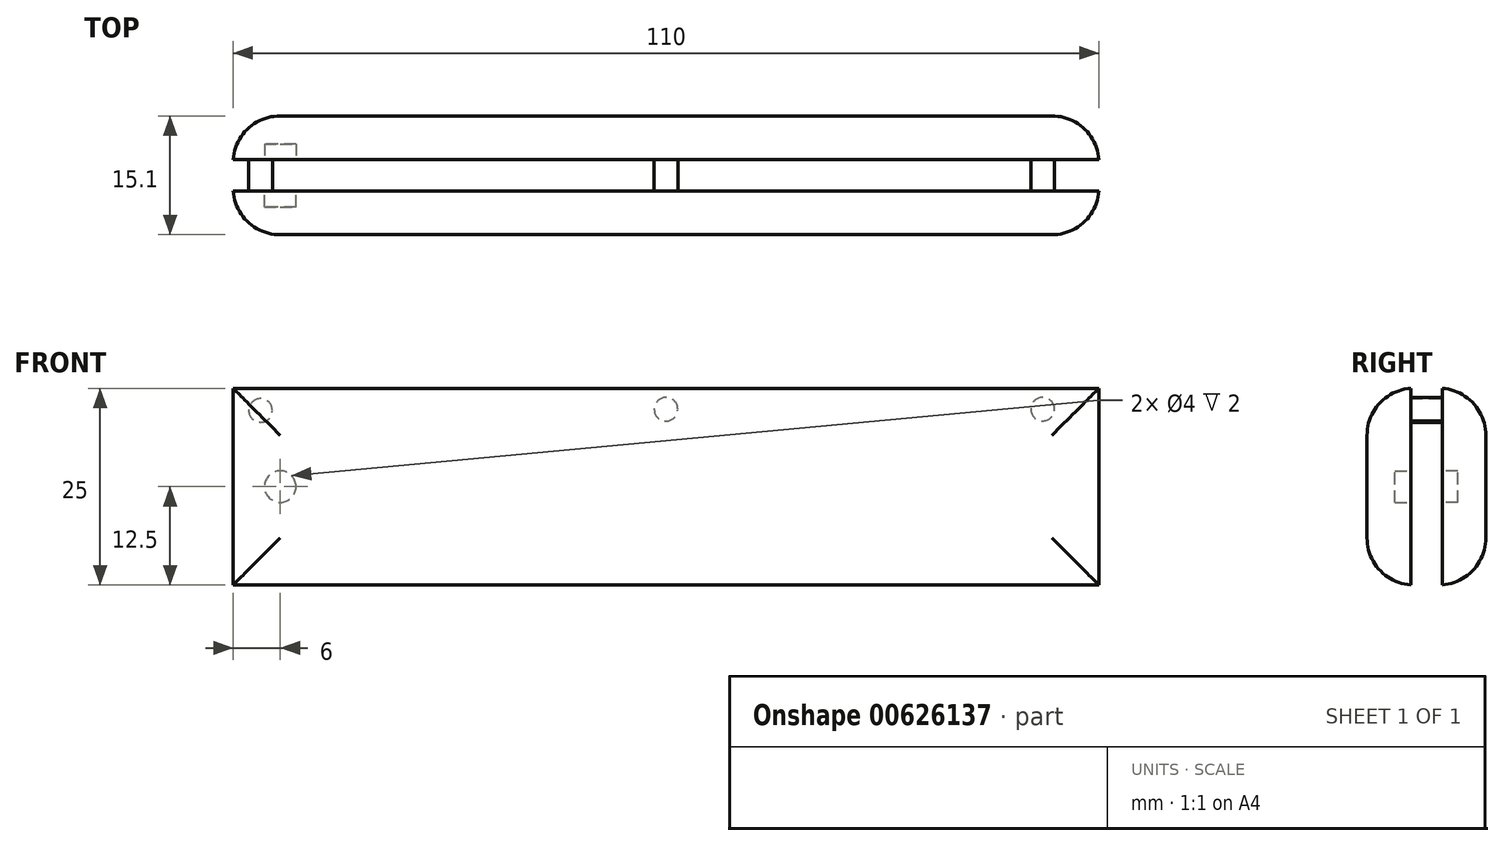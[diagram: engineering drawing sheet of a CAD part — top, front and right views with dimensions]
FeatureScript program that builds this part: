
annotation { "Feature Type Name" : "Feature", "Feature Type Description" : "" }
export const myFeature = defineFeature(function(context is Context, id is Id, definition is map)
    precondition{}
    {
        {
            var Q0;
            Q0=qCreatedBy(makeId("Front.planeOp"),FACE);
            var sketch = newSketch(context, id + "F0", { "sketchPlane" : qUnion([Q0])});
            skLineSegment(sketch, "E0.bottom", {"start": v(55, -12.5) * mm, "end": v(-55, -12.5) * mm});
            skLineSegment(sketch, "E0.top", {"start": v(55, 12.5) * mm, "end": v(-55, 12.5) * mm});
            skLineSegment(sketch, "E0.left", {"start": v(55, -12.5) * mm, "end": v(55, 12.5) * mm});
            skLineSegment(sketch, "E0.right", {"start": v(-55, -12.5) * mm, "end": v(-55, 12.5) * mm});
            skPoint(sketch, "E0.middle", {"position": v(0, 0) * mm});
            skSolve(sketch);
        }
        {
            var Q0;
            Q0 = qSketchRegion(id + "F0", true);
            extrude(context, id + "F1", {"entities" : qUnion([Q0]), "depth" : 5.55 * mm, "offsetDistance" : 25 * mm});
        }
        {
            var Q0;
            Q0=makeQuery(id+"F1.opExtrude","CAP_FACE",FACE,{"disambiguationData":[OSD([sQuery(id+"F0.wireOp",EDGE,"E0.bottom"),sQuery(id+"F0.wireOp",EDGE,"E0.top"),sQuery(id+"F0.wireOp",EDGE,"E0.left"),sQuery(id+"F0.wireOp",EDGE,"E0.right")])],"isStart":false});
            var sketch = newSketch(context, id + "F2", { "sketchPlane" : qUnion([Q0])});
            skCircle(sketch, "E1", {"center": v(-49, 0) * mm, "radius": 2 * mm});
            skSolve(sketch);
        }
        {
            var Q0;
            Q0 = qSketchRegion(id + "F2", true);
            extrude(context, id + "F3", {"entities" : qUnion([Q0]), "operationType" : NewBodyOperationType.REMOVE, "oppositeDirection" : true, "depth" : 2 * mm, "offsetDistance" : 25 * mm});
        }
        {
            var Q0;
            Q0=makeQuery(id+"F1.opExtrude","CAP_FACE",FACE,{"disambiguationData":[OSD([sQuery(id+"F0.wireOp",EDGE,"E0.bottom"),sQuery(id+"F0.wireOp",EDGE,"E0.top"),sQuery(id+"F0.wireOp",EDGE,"E0.left"),sQuery(id+"F0.wireOp",EDGE,"E0.right")])],"isStart":false});
            var sketch = newSketch(context, id + "F4", { "sketchPlane" : qUnion([Q0])});
            skCircle(sketch, "E2", {"center": v(0, 9.82) * mm, "radius": 1.5 * mm});
            skCircle(sketch, "E3", {"center": v(-51.5, 9.67) * mm, "radius": 1.5 * mm});
            skCircle(sketch, "E4", {"center": v(47.84, 9.84) * mm, "radius": 1.5 * mm});
            skSolve(sketch);
        }
        {
            var Q0;
            Q0 = qSketchRegion(id + "F4", true);
            extrude(context, id + "F5", {"entities" : qUnion([Q0]), "operationType" : NewBodyOperationType.ADD, "depth" : 1 * mm, "offsetDistance" : 25 * mm});
        }
        {
            var Q0;
            Q0 = qSketchRegion(id + "F4", true);
            extrude(context, id + "F6", {"entities" : qUnion([Q0]), "operationType" : NewBodyOperationType.ADD, "depth" : 2 * mm, "offsetDistance" : 25 * mm});
        }
        {
            var Q0;
            Q0=makeQuery(id+"F1.opExtrude","SWEPT_BODY",BODY,{"disambiguationData":[OSD([sQuery(id+"F0.wireOp",EDGE,"E0.bottom"),sQuery(id+"F0.wireOp",EDGE,"E0.top"),sQuery(id+"F0.wireOp",EDGE,"E0.left"),sQuery(id+"F0.wireOp",EDGE,"E0.right")])]});
            var Q1;
            Q1=makeQuery(id+"F6.opExtrude","CAP_FACE",FACE,{"disambiguationData":[OSD([sQuery(id+"F4.wireOp",EDGE,"E2")])],"isStart":false});
            mirror(context, id + "F7", {"operationType" : NewBodyOperationType.ADD, "entities" : qUnion([Q0]), "mirrorPlane" : qUnion([Q1])});
        }
        {
            var Q0;
            Q0=makeQuery(id+"F7.opPattern","COPY",FACE,{"derivedFrom":makeQuery(id+"F1.opExtrude","CAP_FACE",FACE,{"disambiguationData":[OSD([sQuery(id+"F0.wireOp",EDGE,"E0.bottom"),sQuery(id+"F0.wireOp",EDGE,"E0.top"),sQuery(id+"F0.wireOp",EDGE,"E0.left"),sQuery(id+"F0.wireOp",EDGE,"E0.right")])],"isStart":true}),"instanceName":"1"});
            var Q1;
            Q1=makeQuery(id+"F1.opExtrude","CAP_FACE",FACE,{"disambiguationData":[OSD([sQuery(id+"F0.wireOp",EDGE,"E0.bottom"),sQuery(id+"F0.wireOp",EDGE,"E0.top"),sQuery(id+"F0.wireOp",EDGE,"E0.left"),sQuery(id+"F0.wireOp",EDGE,"E0.right")])],"isStart":true});
            fillet(context, id + "F8", {"entities" : qUnion([Q0, Q1]), "radius" : 6 * mm, "tangentPropagation" : true, "allowEdgeOverflow" : false});
        }
    });
